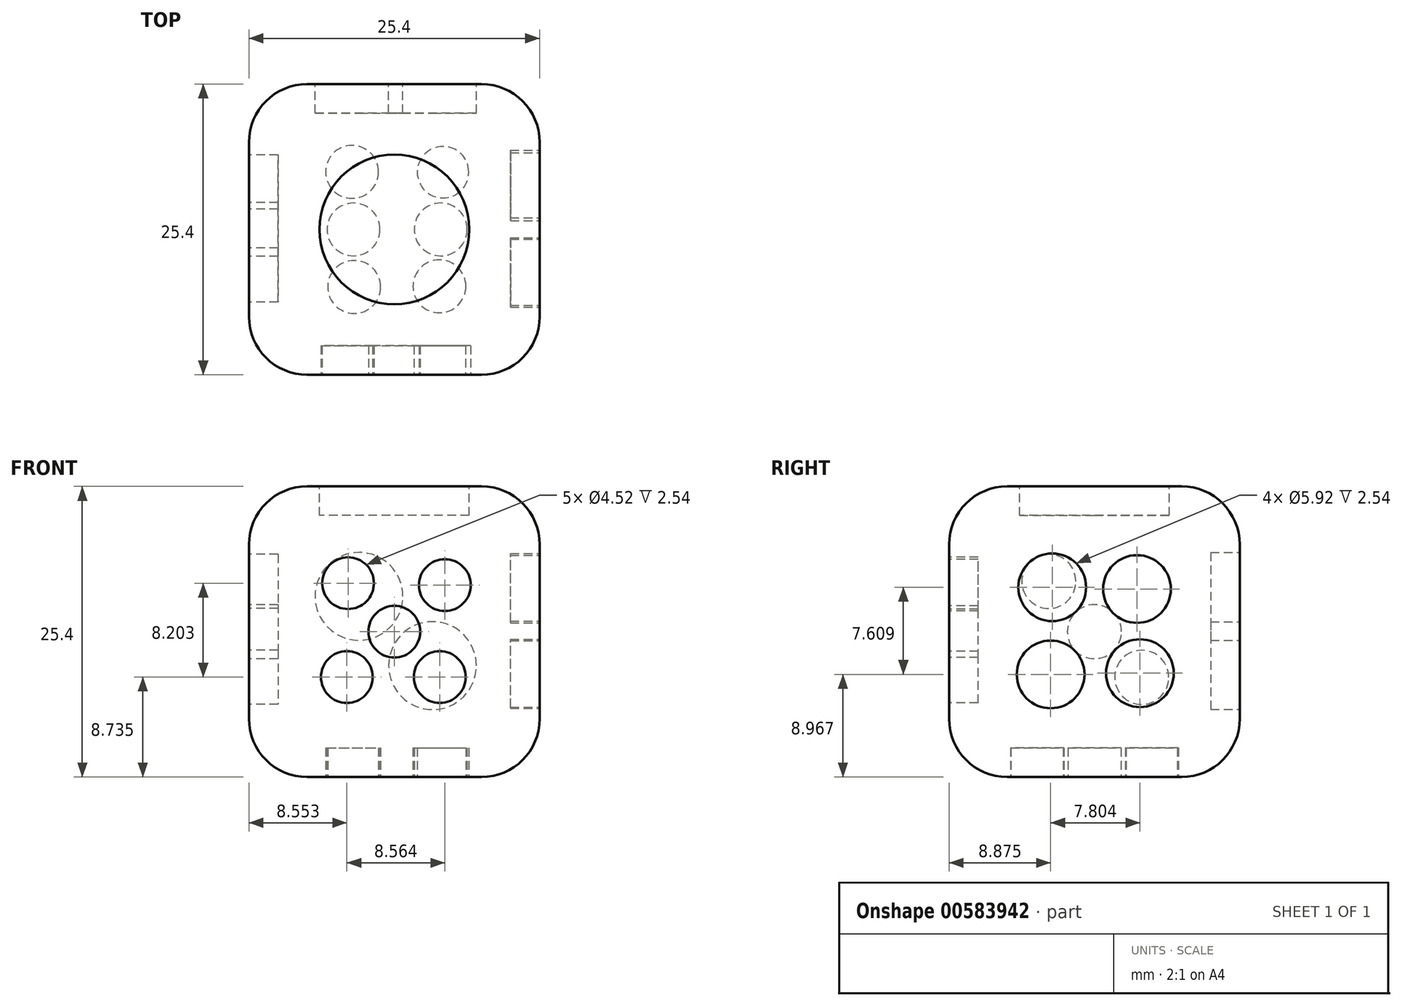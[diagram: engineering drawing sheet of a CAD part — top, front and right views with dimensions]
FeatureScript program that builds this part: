
annotation { "Feature Type Name" : "Feature", "Feature Type Description" : "" }
export const myFeature = defineFeature(function(context is Context, id is Id, definition is map)
    precondition{}
    {
        {
            var Q0;
            Q0=qCreatedBy(makeId("Front.planeOp"),FACE);
            var sketch = newSketch(context, id + "F0", { "sketchPlane" : qUnion([Q0])});
            skLineSegment(sketch, "E0.bottom", {"start": v(12.7, 12.7) * mm, "end": v(-12.7, 12.7) * mm});
            skLineSegment(sketch, "E0.top", {"start": v(12.7, -12.7) * mm, "end": v(-12.7, -12.7) * mm});
            skLineSegment(sketch, "E0.left", {"start": v(12.7, 12.7) * mm, "end": v(12.7, -12.7) * mm});
            skLineSegment(sketch, "E0.right", {"start": v(-12.7, 12.7) * mm, "end": v(-12.7, -12.7) * mm});
            skPoint(sketch, "E0.middle", {"position": v(0, 0) * mm});
            skSolve(sketch);
        }
        {
            var Q0;
            Q0=makeQuery(id+"F0.imprint","IMPRINT",FACE,{"disambiguationData":[TD([[makeQuery(id+"F0.imprint","IMPRINT",EDGE,{"derivedFrom":sQuery(id+"F0.wireOp",EDGE,"E0.bottom")}),1.0]])]});
            extrude(context, id + "F1", {"entities" : qUnion([Q0]), "depth" : 12.7 * mm, "offsetDistance" : 25.4 * mm});
        }
        {
            var Q0;
            Q0=makeQuery(id+"F1.opExtrude","CAP_FACE",FACE,{"disambiguationData":[OSD([sQuery(id+"F0.wireOp",EDGE,"E0.bottom"),sQuery(id+"F0.wireOp",EDGE,"E0.top"),sQuery(id+"F0.wireOp",EDGE,"E0.left"),sQuery(id+"F0.wireOp",EDGE,"E0.right")])],"isStart":true});
            extrude(context, id + "F2", {"entities" : qUnion([Q0]), "operationType" : NewBodyOperationType.ADD, "depth" : 12.7 * mm, "offsetDistance" : 25.4 * mm});
        }
        {
            var Q0;
            Q0=makeQuery(id+"F1.opExtrude","CAP_EDGE",EDGE,{"disambiguationData":[OSD([sQuery(id+"F0.wireOp",EDGE,"E0.bottom")])],"isStart":false});
            var Q1;
            Q1=makeQuery(id+"F1.opExtrude","CAP_EDGE",EDGE,{"disambiguationData":[OSD([sQuery(id+"F0.wireOp",EDGE,"E0.right")])],"isStart":false});
            var Q2;
            Q2=makeQuery(id+"F1.opExtrude","CAP_EDGE",EDGE,{"disambiguationData":[OSD([sQuery(id+"F0.wireOp",EDGE,"E0.left")])],"isStart":false});
            var Q3;
            {var subQ0=sQuery(id+"F0.wireOp",EDGE,"E0.left");var subQ1=sQuery(id+"F0.wireOp",EDGE,"E0.bottom");Q3=makeQuery(id+"F2.boolean.opBoolean","MERGE",EDGE,{"derivedFrom":[makeQuery(id+"F1.opExtrude","SWEPT_EDGE",EDGE,{"disambiguationData":[OSD([subQ1,subQ0])]}),makeQuery(id+"F2.opExtrude","SWEPT_EDGE",EDGE,{"disambiguationData":[OSD([subQ1,subQ0])]})]});}
            var Q4;
            Q4=makeQuery(id+"F1.opExtrude","CAP_EDGE",EDGE,{"disambiguationData":[OSD([sQuery(id+"F0.wireOp",EDGE,"E0.top")])],"isStart":false});
            var Q5;
            {var subQ0=sQuery(id+"F0.wireOp",EDGE,"E0.right");var subQ1=sQuery(id+"F0.wireOp",EDGE,"E0.top");Q5=makeQuery(id+"F2.boolean.opBoolean","MERGE",EDGE,{"derivedFrom":[makeQuery(id+"F1.opExtrude","SWEPT_EDGE",EDGE,{"disambiguationData":[OSD([subQ1,subQ0])]}),makeQuery(id+"F2.opExtrude","SWEPT_EDGE",EDGE,{"disambiguationData":[OSD([subQ1,subQ0])]})]});}
            var Q6;
            {var subQ0=sQuery(id+"F0.wireOp",EDGE,"E0.left");var subQ1=sQuery(id+"F0.wireOp",EDGE,"E0.top");Q6=makeQuery(id+"F2.boolean.opBoolean","MERGE",EDGE,{"derivedFrom":[makeQuery(id+"F1.opExtrude","SWEPT_EDGE",EDGE,{"disambiguationData":[OSD([subQ1,subQ0])]}),makeQuery(id+"F2.opExtrude","SWEPT_EDGE",EDGE,{"disambiguationData":[OSD([subQ1,subQ0])]})]});}
            var Q7;
            {var subQ0=sQuery(id+"F0.wireOp",EDGE,"E0.right");var subQ1=sQuery(id+"F0.wireOp",EDGE,"E0.bottom");Q7=makeQuery(id+"F2.boolean.opBoolean","MERGE",EDGE,{"derivedFrom":[makeQuery(id+"F1.opExtrude","SWEPT_EDGE",EDGE,{"disambiguationData":[OSD([subQ1,subQ0])]}),makeQuery(id+"F2.opExtrude","SWEPT_EDGE",EDGE,{"disambiguationData":[OSD([subQ1,subQ0])]})]});}
            var Q8;
            Q8=makeQuery(id+"F2.opExtrude","CAP_EDGE",EDGE,{"disambiguationData":[OSD([sQuery(id+"F0.wireOp",EDGE,"E0.right")])],"isStart":false});
            var Q9;
            Q9=makeQuery(id+"F2.opExtrude","CAP_EDGE",EDGE,{"disambiguationData":[OSD([sQuery(id+"F0.wireOp",EDGE,"E0.top")])],"isStart":false});
            var Q10;
            Q10=makeQuery(id+"F2.opExtrude","CAP_EDGE",EDGE,{"disambiguationData":[OSD([sQuery(id+"F0.wireOp",EDGE,"E0.left")])],"isStart":false});
            var Q11;
            Q11=makeQuery(id+"F2.opExtrude","CAP_EDGE",EDGE,{"disambiguationData":[OSD([sQuery(id+"F0.wireOp",EDGE,"E0.bottom")])],"isStart":false});
            fillet(context, id + "F3", {"entities" : qUnion([Q0, Q1, Q2, Q3, Q4, Q5, Q6, Q7, Q8, Q9, Q10, Q11]), "radius" : 5.08 * mm, "tangentPropagation" : true, "allowEdgeOverflow" : false});
        }
        {
            var Q0;
            Q0=makeQuery(id+"F1.opExtrude","CAP_FACE",FACE,{"disambiguationData":[OSD([sQuery(id+"F0.wireOp",EDGE,"E0.bottom"),sQuery(id+"F0.wireOp",EDGE,"E0.top"),sQuery(id+"F0.wireOp",EDGE,"E0.left"),sQuery(id+"F0.wireOp",EDGE,"E0.right")])],"isStart":false});
            var sketch = newSketch(context, id + "F4", { "sketchPlane" : qUnion([Q0])});
            skCircle(sketch, "E1", {"center": v(0, 0) * mm, "radius": 2.26 * mm});
            skCircle(sketch, "E2", {"center": v(-4.04, 4.24) * mm, "radius": 2.26 * mm});
            skCircle(sketch, "E3", {"center": v(4.42, 4.07) * mm, "radius": 2.26 * mm});
            skCircle(sketch, "E4", {"center": v(-4.15, -3.96) * mm, "radius": 2.26 * mm});
            skCircle(sketch, "E5", {"center": v(3.98, -3.96) * mm, "radius": 2.26 * mm});
            skSolve(sketch);
        }
        {
            var Q0;
            Q0=makeQuery(id+"F2.opExtrude","CAP_FACE",FACE,{"disambiguationData":[OSD([sQuery(id+"F0.wireOp",EDGE,"E0.bottom"),sQuery(id+"F0.wireOp",EDGE,"E0.top"),sQuery(id+"F0.wireOp",EDGE,"E0.left"),sQuery(id+"F0.wireOp",EDGE,"E0.right")])],"isStart":false});
            var sketch = newSketch(context, id + "F5", { "sketchPlane" : qUnion([Q0])});
            skCircle(sketch, "E6", {"center": v(3.09, 3.09) * mm, "radius": 3.84 * mm});
            skCircle(sketch, "E7", {"center": v(-3.34, -2.97) * mm, "radius": 3.84 * mm});
            skSolve(sketch);
        }
        {
            var Q0;
            {var subQ0=sQuery(id+"F0.wireOp",EDGE,"E0.bottom");Q0=makeQuery(id+"F2.boolean.opBoolean","MERGE",FACE,{"derivedFrom":[makeQuery(id+"F1.opExtrude","SWEPT_FACE",FACE,{"disambiguationData":[OSD([subQ0])]}),makeQuery(id+"F2.opExtrude","SWEPT_FACE",FACE,{"disambiguationData":[OSD([subQ0])]})]});}
            var sketch = newSketch(context, id + "F6", { "sketchPlane" : qUnion([Q0])});
            skCircle(sketch, "E8", {"center": v(0, 0) * mm, "radius": 6.54 * mm});
            skSolve(sketch);
        }
        {
            var Q0;
            {var subQ0=sQuery(id+"F0.wireOp",EDGE,"E0.top");Q0=makeQuery(id+"F2.boolean.opBoolean","MERGE",FACE,{"derivedFrom":[makeQuery(id+"F1.opExtrude","SWEPT_FACE",FACE,{"disambiguationData":[OSD([subQ0])]}),makeQuery(id+"F2.opExtrude","SWEPT_FACE",FACE,{"disambiguationData":[OSD([subQ0])]})]});}
            var sketch = newSketch(context, id + "F7", { "sketchPlane" : qUnion([Q0])});
            skCircle(sketch, "E9", {"center": v(4.05, 0) * mm, "radius": 2.31 * mm});
            skCircle(sketch, "E10", {"center": v(-3.57, 0) * mm, "radius": 2.3 * mm});
            skCircle(sketch, "E11", {"center": v(-3.5, 5.03) * mm, "radius": 2.31 * mm});
            skCircle(sketch, "E12", {"center": v(3.94, 4.97) * mm, "radius": 2.31 * mm});
            skCircle(sketch, "E13", {"center": v(-3.69, -5.03) * mm, "radius": 2.3 * mm});
            skCircle(sketch, "E14", {"center": v(4.26, -5) * mm, "radius": 2.25 * mm});
            skSolve(sketch);
        }
        {
            var Q0;
            {var subQ0=sQuery(id+"F0.wireOp",EDGE,"E0.right");Q0=makeQuery(id+"F2.boolean.opBoolean","MERGE",FACE,{"derivedFrom":[makeQuery(id+"F1.opExtrude","SWEPT_FACE",FACE,{"disambiguationData":[OSD([subQ0])]}),makeQuery(id+"F2.opExtrude","SWEPT_FACE",FACE,{"disambiguationData":[OSD([subQ0])]})]});}
            var sketch = newSketch(context, id + "F8", { "sketchPlane" : qUnion([Q0])});
            skCircle(sketch, "E15", {"center": v(0, 0) * mm, "radius": 2.36 * mm});
            skCircle(sketch, "E16", {"center": v(3.98, 4.4) * mm, "radius": 2.36 * mm});
            skCircle(sketch, "E17", {"center": v(-4.14, -4) * mm, "radius": 2.36 * mm});
            skSolve(sketch);
        }
        {
            var Q0;
            {var subQ0=sQuery(id+"F0.wireOp",EDGE,"E0.left");Q0=makeQuery(id+"F2.boolean.opBoolean","MERGE",FACE,{"derivedFrom":[makeQuery(id+"F1.opExtrude","SWEPT_FACE",FACE,{"disambiguationData":[OSD([subQ0])]}),makeQuery(id+"F2.opExtrude","SWEPT_FACE",FACE,{"disambiguationData":[OSD([subQ0])]})]});}
            var sketch = newSketch(context, id + "F9", { "sketchPlane" : qUnion([Q0])});
            skCircle(sketch, "E18", {"center": v(-3.69, 3.88) * mm, "radius": 2.96 * mm});
            skCircle(sketch, "E19", {"center": v(3.73, 3.73) * mm, "radius": 2.96 * mm});
            skCircle(sketch, "E20", {"center": v(-3.82, -3.73) * mm, "radius": 2.96 * mm});
            skCircle(sketch, "E21", {"center": v(3.98, -3.63) * mm, "radius": 2.96 * mm});
            skSolve(sketch);
        }
        {
            var Q0;
            Q0=makeQuery(id+"F7.imprint","IMPRINT",FACE,{"disambiguationData":[TD([[makeQuery(id+"F7.imprint","IMPRINT",EDGE,{"derivedFrom":sQuery(id+"F7.wireOp",EDGE,"E13")}),1.0]])]});
            var Q1;
            Q1=makeQuery(id+"F7.imprint","IMPRINT",FACE,{"disambiguationData":[TD([[makeQuery(id+"F7.imprint","IMPRINT",EDGE,{"derivedFrom":sQuery(id+"F7.wireOp",EDGE,"E10")}),1.0]])]});
            var Q2;
            Q2=makeQuery(id+"F7.imprint","IMPRINT",FACE,{"disambiguationData":[TD([[makeQuery(id+"F7.imprint","IMPRINT",EDGE,{"derivedFrom":sQuery(id+"F7.wireOp",EDGE,"E14")}),1.0]])]});
            var Q3;
            Q3=makeQuery(id+"F7.imprint","IMPRINT",FACE,{"disambiguationData":[TD([[makeQuery(id+"F7.imprint","IMPRINT",EDGE,{"derivedFrom":sQuery(id+"F7.wireOp",EDGE,"E9")}),1.0]])]});
            var Q4;
            Q4=makeQuery(id+"F7.imprint","IMPRINT",FACE,{"disambiguationData":[TD([[makeQuery(id+"F7.imprint","IMPRINT",EDGE,{"derivedFrom":sQuery(id+"F7.wireOp",EDGE,"E12")}),1.0]])]});
            var Q5;
            Q5=makeQuery(id+"F7.imprint","IMPRINT",FACE,{"disambiguationData":[TD([[makeQuery(id+"F7.imprint","IMPRINT",EDGE,{"derivedFrom":sQuery(id+"F7.wireOp",EDGE,"E11")}),1.0]])]});
            extrude(context, id + "F10", {"entities" : qUnion([Q0, Q1, Q2, Q3, Q4, Q5]), "operationType" : NewBodyOperationType.REMOVE, "oppositeDirection" : true, "depth" : 2.54 * mm, "offsetDistance" : 25.4 * mm});
        }
        {
            var Q0;
            Q0=makeQuery(id+"F6.imprint","IMPRINT",FACE,{"disambiguationData":[TD([[makeQuery(id+"F6.imprint","IMPRINT",EDGE,{"derivedFrom":sQuery(id+"F6.wireOp",EDGE,"E8")}),1.0]])]});
            extrude(context, id + "F11", {"entities" : qUnion([Q0]), "operationType" : NewBodyOperationType.REMOVE, "oppositeDirection" : true, "depth" : 2.54 * mm, "offsetDistance" : 25.4 * mm});
        }
        {
            var Q0;
            Q0 = qSketchRegion(id + "F4", true);
            extrude(context, id + "F12", {"entities" : qUnion([Q0]), "operationType" : NewBodyOperationType.REMOVE, "oppositeDirection" : true, "depth" : 2.54 * mm, "offsetDistance" : 25.4 * mm});
        }
        {
            var Q0;
            Q0 = qSketchRegion(id + "F5", true);
            extrude(context, id + "F13", {"entities" : qUnion([Q0]), "operationType" : NewBodyOperationType.REMOVE, "oppositeDirection" : true, "depth" : 2.54 * mm, "offsetDistance" : 25.4 * mm});
        }
        {
            var Q0;
            Q0 = qSketchRegion(id + "F8", true);
            extrude(context, id + "F14", {"entities" : qUnion([Q0]), "operationType" : NewBodyOperationType.REMOVE, "oppositeDirection" : true, "depth" : 2.54 * mm, "offsetDistance" : 25.4 * mm});
        }
        {
            var Q0;
            Q0 = qSketchRegion(id + "F9", true);
            extrude(context, id + "F15", {"entities" : qUnion([Q0]), "operationType" : NewBodyOperationType.REMOVE, "oppositeDirection" : true, "depth" : 2.54 * mm, "offsetDistance" : 25.4 * mm});
        }
    });
